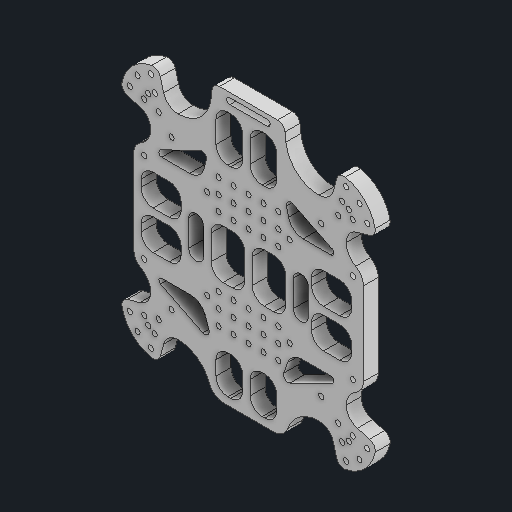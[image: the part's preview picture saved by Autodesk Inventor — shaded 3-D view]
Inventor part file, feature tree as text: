
AUTODESK INVENTOR PART (.ipt)
format: ipt  version: 2023 (Build 270158000, 158)  size: 730,112 bytes
history: native  units: mm
features: reference x147, extrude x5, fillet x4, sketch x4, other x4, plane x1
ambient origin geometry x8: Origin, YZ Plane, XZ Plane, XY Plane, X Axis, Y Axis, Z Axis, Center Point
bodies: Solid1 (feature_tree)
feature tree (165):
  plane  "Work Plane1"
  extrude  "Extrusion1"  Depth=10.0mm
  extrude  "Extrusion2"  Depth=10.0mm TaperAngle=0.0deg
  fillet  "Fillet1"  Radius=5.0mm
  extrude  "Extrusion3"  Depth=5.0mm
  extrude  "Extrusion4"  Depth=5.0mm
  extrude  "Extrusion5"  Depth=5.0mm
  fillet  "Fillet2"  Radius=5.0mm
  fillet  "Fillet3"  Radius=5.0mm
  fillet  "Fillet4"  Radius=5.0mm
  reference  "Reference1"
  reference  "Reference2"
  reference  "Reference3"
  reference  "Reference4"
  reference  "Reference5"
  reference  "Reference6"
  reference  "Reference7"
  reference  "Reference8"
  reference  "Reference9"
  reference  "Reference10"
  reference  "Reference11"
  reference  "Reference12"
  reference  "Reference13"
  reference  "Reference14"
  reference  "Reference15"
  reference  "Reference16"
  reference  "Reference17"
  reference  "Reference18"
  reference  "Reference19"
  reference  "Reference20"
  reference  "Reference21"
  reference  "Reference22"
  reference  "Reference23"
  reference  "Reference24"
  reference  "Reference25"
  reference  "Reference26"
  reference  "Reference27"
  reference  "Reference28"
  reference  "Reference29"
  reference  "Reference30"
  reference  "Reference31"
  reference  "Reference32"
  reference  "Reference33"
  reference  "Reference34"
  reference  "Reference35"
  reference  "Reference36"
  reference  "Reference37"
  reference  "Reference38"
  reference  "Reference39"
  reference  "Reference40"
  reference  "Reference41"
  reference  "Reference42"
  reference  "Reference43"
  reference  "Reference44"
  reference  "Reference45"
  reference  "Reference46"
  reference  "Reference47"
  reference  "Reference48"
  reference  "Reference49"
  reference  "Reference50"
  reference  "Reference51"
  reference  "Reference52"
  reference  "Reference53"
  reference  "Reference54"
  reference  "Reference55"
  reference  "Reference56"
  reference  "Reference57"
  reference  "Reference58"
  reference  "Reference59"
  reference  "Reference60"
  reference  "Reference61"
  reference  "Reference62"
  reference  "Reference63"
  reference  "Reference64"
  reference  "Reference65"
  reference  "Reference66"
  reference  "Reference67"
  reference  "Reference68"
  reference  "Reference69"
  reference  "Reference70"
  reference  "Reference71"
  reference  "Reference72"
  reference  "Reference73"
  reference  "Reference74"
  reference  "Reference75"
  reference  "Reference76"
  reference  "Reference77"
  reference  "Reference78"
  reference  "Reference79"
  reference  "Reference80"
  reference  "Reference81"
  reference  "Reference82"
  reference  "Reference83"
  reference  "Reference84"
  reference  "Reference85"
  reference  "Reference86"
  reference  "Reference87"
  reference  "Reference88"
  reference  "Reference89"
  reference  "Reference90"
  reference  "Reference91"
  reference  "Reference92"
  reference  "Reference93"
  reference  "Reference94"
  reference  "Reference95"
  reference  "Reference96"
  reference  "Reference97"
  reference  "Reference98"
  reference  "Reference99"
  reference  "Reference100"
  reference  "Reference101"
  reference  "Reference102"
  reference  "Reference103"
  reference  "Reference104"
  reference  "Reference105"
  reference  "Reference106"
  reference  "Reference107"
  reference  "Reference108"
  reference  "Reference109"
  reference  "Reference110"
  reference  "Reference111"
  reference  "Reference112"
  reference  "Reference113"
  reference  "Reference114"
  reference  "Reference115"
  reference  "Reference116"
  reference  "Reference117"
  reference  "Reference118"
  reference  "Reference119"
  reference  "Reference120"
  reference  "Reference121"
  reference  "Reference122"
  reference  "Reference123"
  reference  "Reference124"
  reference  "Reference125"
  reference  "Reference126"
  reference  "Reference127"
  reference  "Reference128"
  sketch  "Sketch2"  dims[d6=3.5mm d7=30.0mm d9=10.0mm d10=50.0mm d12=10.0mm]
  reference  "Reference129"
  reference  "Reference130"
  reference  "Reference131"
  reference  "Reference132"
  reference  "Reference133"
  reference  "Reference134"
  reference  "Reference135"
  reference  "Reference136"
  reference  "Reference137"
  reference  "Reference138"
  reference  "Reference139"
  reference  "Reference140"
  reference  "Reference141"
  reference  "Reference142"
  reference  "Reference143"
  reference  "Reference144"
  reference  "Reference145"
  reference  "Reference146"
  reference  "Reference147"
  sketch  "Sketch3"  dims[d15=30.0mm d17=10.0mm d18=50.0mm d20=10.0mm d23=10.0mm d24=0.0mm d25=5.0mm]
  sketch  "Sketch4"  dims[d27=5.0mm d28=5.0mm]
  sketch  "Sketch5"  dims[d29=5.0mm d30=5.0mm d31=5.0mm d33=5.0mm d34=5.0mm d35=5.0mm d36=5.0mm d37=10.0mm d38=5.0mm d40=5.0mm d41=5.0mm d42=2.0mm d43=10.0mm d44=0.0mm d45=8.0mm d46=100.0mm d47=100.0mm d48=3.5mm d49=10.0mm d50=0.0mm d51=6.5mm d52=6.5mm d58=50.0mm d60=10.0mm d61=30.0mm d63=10.0mm d66=50.0mm d68=10.0mm d69=30.0mm d71=10.0mm d74=3.0mm d75=0.0mm d76=70.0mm d77=5.0mm d78=5.0mm d79=5.0mm d80=35.0mm d81=60.0mm d82=5.0mm d83=3.0mm d84=0.0mm d85=3.0mm d86=10.0mm d87=2.0mm]
  parser-record x1  (decoder bookkeeping rows leaked as tree rows — omitted from the tree; the rows remain in map.json)
  other  "total.iam"
  other  "bottom:1"
  other  "middle spacer top:1"
note: 1 file-system path scrubbed to <path> (originals preserved in map.json)
